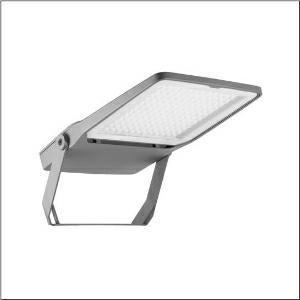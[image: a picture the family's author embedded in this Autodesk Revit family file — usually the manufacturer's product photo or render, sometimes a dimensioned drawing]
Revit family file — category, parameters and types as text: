
# Revit family: floodlight_fl_20_midi___pl61_5xa7682d1c1ac_5419
name_source: partatom
category: Lighting Fixtures
units: mm (PartAtom-declared; Revit-internal decimal feet)

## family parameters
Cut with Voids When Loaded = No
Host = Face
Light Source = No
Part Type = Normal
Room Calculation Point = No
Round Connector Dimension = Use Diameter
Shared = No

## types (1)
- --- (1 x LED 3000K / CRI = 80 (unbekannt), 14290 lm, 3000K)
    Apparent Load = 142 VA
    CIE Flux Codes = 33 65 98 100 100
    Color Rendering = 80
    Color Temperature = 3000K
    Default Elevation = 1800 mm
    Description = Floodlight FL 20 midi, floodlight, primary light control with lens, of plastic, primary optical cover: protective disc, of toughened safety glass, transparent, light distribution: PL61, light emission: direct distribution, primary light characteristic: asymmetric, installation type: surface-mounted, LED High Power LED, rated luminous flux: 14.290 lm, light colour: 830, colour temperature: 3000K, control gear: ECG Plus, control: digital communication interface, time-dependent luminous flux control, flexible luminous flux parameterisation, power reduction, overheat protection, electronic power reduction, with terminal, 5-pole, max. 2.5mm², mains connection: 220..240V, AC, 50/60Hz, rated input power: 142W, LED unit, of diecast aluminium, powder-coated, Siteco® metallic grey (DB 702S), length: 654 mm, width: 450 mm, height: 76mm, housing frame, of diecast aluminium, powder-coated, Siteco® metallic grey (DB 702S), mounting bracket, of steel, powder-coated, Siteco® metallic grey (DB 702S), DALIprotection rating (complete): IP66, insulation class (complete): insulation class II (safety insulation), certification: CE, ENEC, VDE, protection symbol: D, permissible ambient temperature for indoor applications: -40..+40°C, permissible ambient temperature for outdoor applications: -40..+50°C, standard: DIN EN 12944, packaging unit: 1 piece

Light Distribution: PL61
    Height = 76 mm
    Lamp = 1 x LED 3000K / CRI >= 80 (unbekannt)
    Lamp Light Flux = 14290 lm
    Lamp count = 1
    Length = 672 mm
    Luminous efficacy = 101 lm/W
    Manufacturer = Siteco
    ModVariant = No
    Model = 5XA7682D1C1AC
    Number of Poles = 1
    OnlyDefault = Yes
    Power Factor = 1
    Product Name = Floodlight FL 20 midi | PL61
    Product group = floodlight | pylon top
    ProductGroupID = 6101
    Protection Class = Protection class II
    Protection Degree = IP 66
    RLX_Detail_Level = 1
    RlxData = <blob elided: 97929 chars, md5=12c1328d>
    Socket = socket
    Standby Power = 0 W
    System Light Flux = 14290 lm
    System Power = 142 W
    Type Comments = factory setting: luminous flux: 100 % | dim-lin: 254 | 489 mA
    Type Image = l_1005943.jpg
    URL = http://relux.com
    VarID = @adj_142753
    Voltage = 0 V
    Weight = 0.00 kg
    Width = 450 mm

## geometry (parser evidence)
native form markers: Blend x4, Sweep x15
no freeform markers — native parametric forms only
